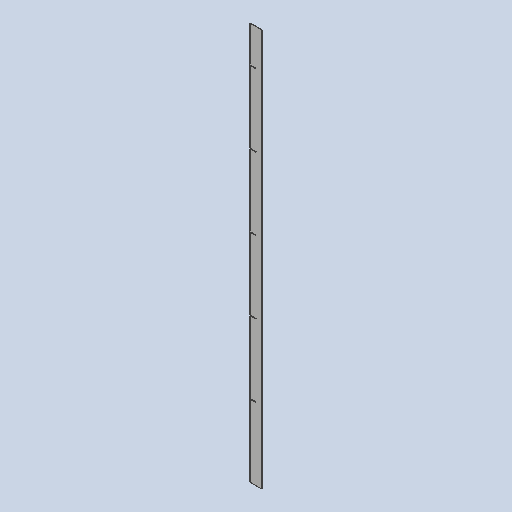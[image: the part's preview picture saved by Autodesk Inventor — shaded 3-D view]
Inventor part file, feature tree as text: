
AUTODESK INVENTOR PART (.ipt)
format: ipt  version: 2025 (Build 290162010, 162A)  size: 151,552 bytes
history: native  units: mm
features: other x3, sketch x2, sheet_metal_op x1, extrude x1, pattern_linear x1, projected_geometry x1
ambient origin geometry x8: Origin, YZ Plane, XZ Plane, XY Plane, X Axis, Y Axis, Z Axis, Center Point
bodies: Body1 (feature_tree)
feature tree (9):
  other  "BSH 042 stringer 2"
  sheet_metal_op  "Face2"
  extrude  "Extrusion2"  Depth=2751.5mm
  pattern_linear  "Rectangular Pattern1"  Spacing1=41.319714mm  [1 undecoded]
  sketch  "Sketch6"  dims[d26=80.639428mm d27=2751.5mm]
  other  "Plate4"
  sketch  "Sketch7"  dims[d28=3.0mm d29=41.319714mm d30=3.2mm d31=498.5mm d32=0.0mm d33=0.0mm d34=50.0mm d36=500.0mm]
  projected_geometry  "Projected Loop1"
  other  "Definition1"
note: 1 required parameter value undecoded (feature->parameter linkage not recoverable at this tier; creation-order binding heuristic only, values carry confidence <= 0.55)
